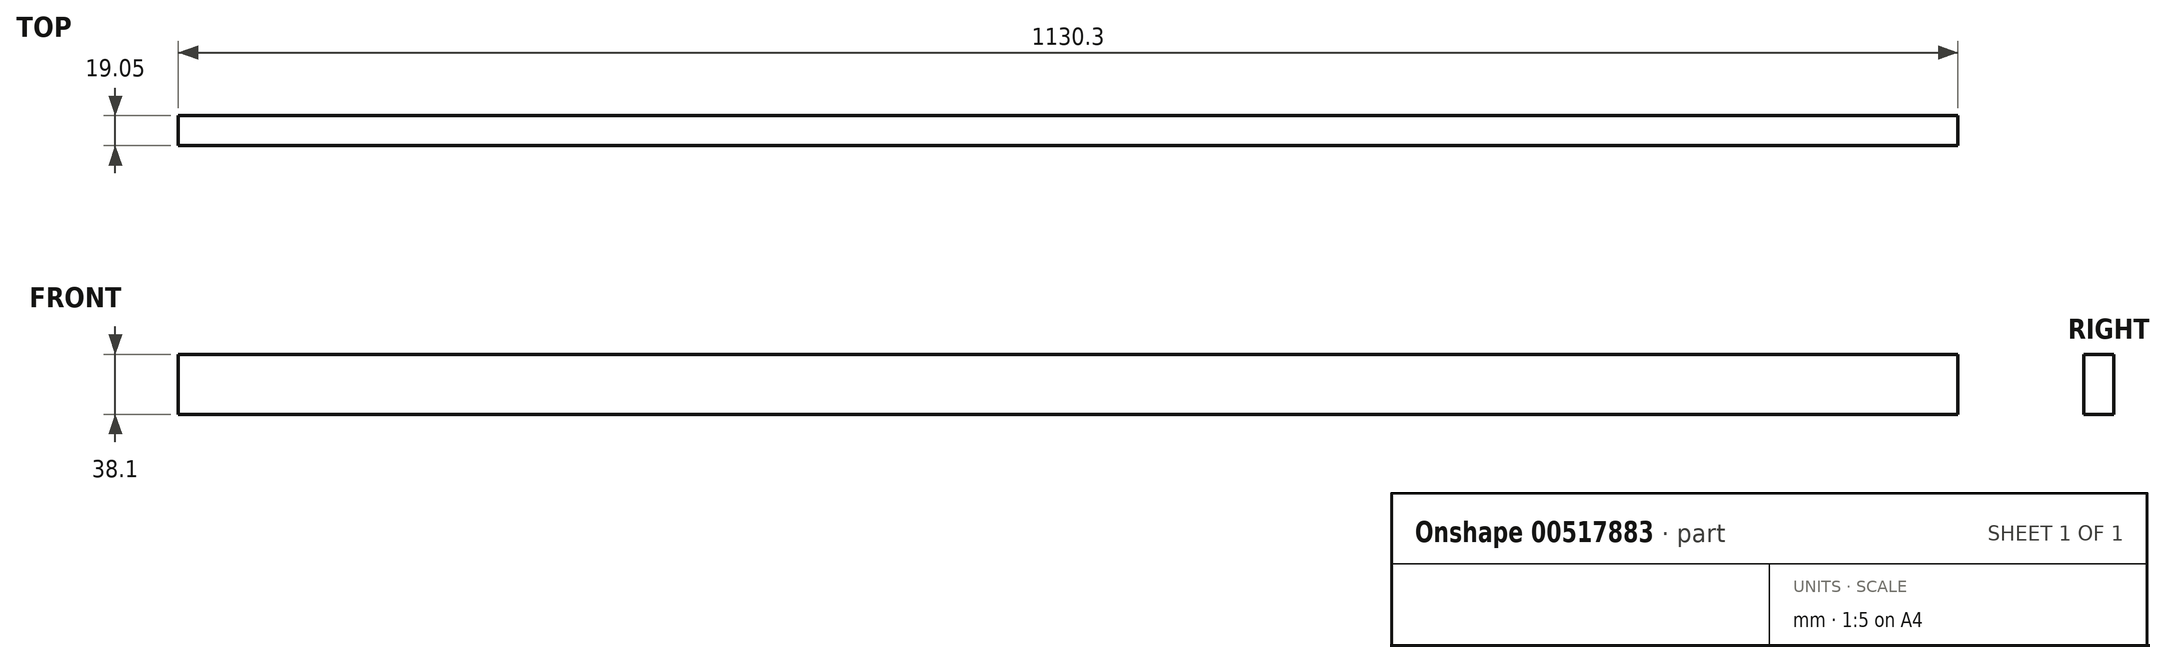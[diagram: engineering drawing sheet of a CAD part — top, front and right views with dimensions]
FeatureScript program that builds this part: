
annotation { "Feature Type Name" : "Feature", "Feature Type Description" : "" }
export const myFeature = defineFeature(function(context is Context, id is Id, definition is map)
    precondition{}
    {
        {
            var Q0;
            Q0=qCreatedBy(makeId("Right.planeOp"),FACE);
            var sketch = newSketch(context, id + "F0", { "sketchPlane" : qUnion([Q0])});
            skLineSegment(sketch, "E0.bottom", {"start": v(0, 0) * mm, "end": v(19.05, 0) * mm});
            skLineSegment(sketch, "E0.top", {"start": v(0, 38.1) * mm, "end": v(19.05, 38.1) * mm});
            skLineSegment(sketch, "E0.left", {"start": v(0, 0) * mm, "end": v(0, 38.1) * mm});
            skLineSegment(sketch, "E0.right", {"start": v(19.05, 0) * mm, "end": v(19.05, 38.1) * mm});
            skSolve(sketch);
        }
        {
            var Q0;
            Q0=makeQuery(id+"F0.imprint","IMPRINT",FACE,{"disambiguationData":[TD([[makeQuery(id+"F0.imprint","IMPRINT",EDGE,{"derivedFrom":sQuery(id+"F0.wireOp",EDGE,"E0.bottom")}),1.0]])]});
            extrude(context, id + "F1", {"entities" : qUnion([Q0]), "oppositeDirection" : true, "depth" : 1130.3 * mm, "offsetDistance" : 25.4 * mm});
        }
    });
